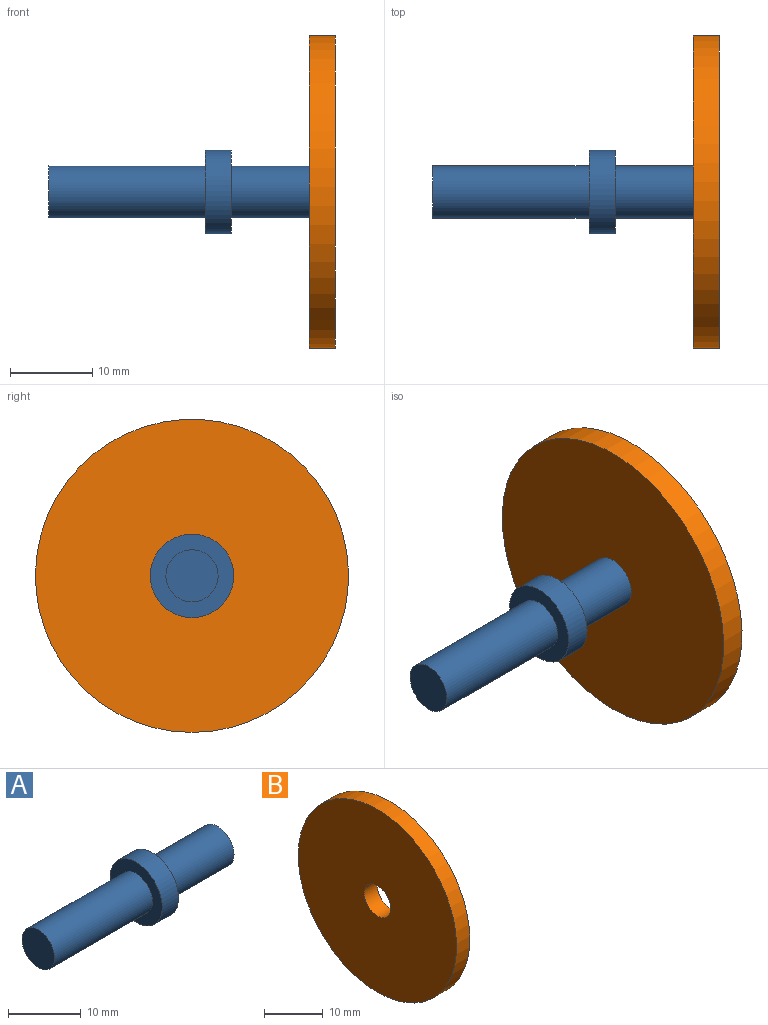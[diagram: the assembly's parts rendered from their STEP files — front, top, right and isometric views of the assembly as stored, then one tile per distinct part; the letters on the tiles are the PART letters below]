
ASSEMBLY  parts=2 mates=1
PART A: 7 faces, bbox 34.9x10.2x10.2 mm
  f0: cylinder r=3.17mm len=19.05mm, axis (1,0,0), area 380mm2, adj f1,f4
  f1: plane 6.35x6.35mm, normal (-1,0,0), area 31.7mm2, adj f0
  f2: cylinder r=5.08mm len=10.16mm, axis (-1,0,0), area 101.3mm2, adj f3,f4
  f3: plane 10.16x10.16mm, normal (1,0,0), area 49.4mm2, adj f2,f5
  f4: plane 10.16x10.16mm, normal (-1,0,0), area 49.4mm2, adj f0,f2
  f5: cylinder r=3.17mm len=12.7mm, axis (-1,0,0), area 253.4mm2, adj f3,f6
  f6: plane 6.35x6.35mm, normal (1,0,0), area 31.7mm2, adj f5
PART B: 4 faces, bbox 3.2x38.1x38.1 mm
  f0: cylinder r=3.17mm len=6.35mm, axis (-1,0,0), area 63.3mm2, adj f2,f3
  f1: cylinder r=19.05mm len=38.1mm, axis (-1,0,0), area 380mm2, adj f2,f3
  f2: plane 38.1x38.1mm, normal (1,0,0), area 1108.4mm2, adj f0,f1
  f3: plane 38.1x38.1mm, normal (-1,0,0), area 1108.4mm2, adj f0,f1
PLACE A t=(-0.77,-0.55,1.22)mm
PLACE B t=(11.93,-0.55,1.22)mm
MATE planar B.f1 <-> A.f5  axis (1,0,0) through (15.11,-0.55,1.22)mm
